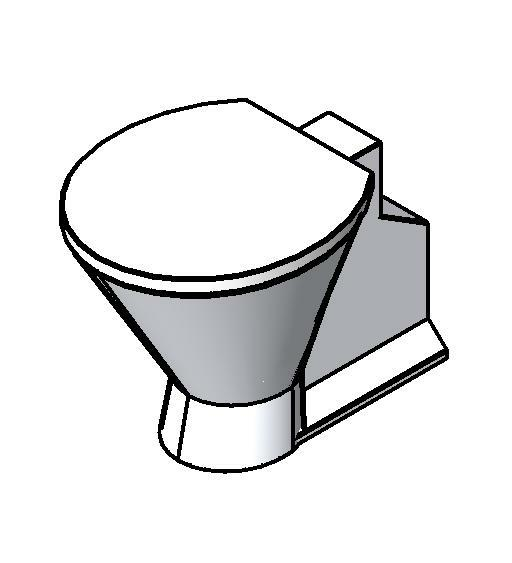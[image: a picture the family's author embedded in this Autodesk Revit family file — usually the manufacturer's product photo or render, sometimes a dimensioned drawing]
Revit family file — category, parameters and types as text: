
# Revit family: Deca_Cuba Semiencaixe retangular 40cm _Cuba Slim_L.63040
name_source: partatom
category: Plumbing Fixtures
units: mm (PartAtom-declared; Revit-internal decimal feet)

## family parameters
Cut with Voids When Loaded = No
Host = Face
Part Type = Normal
Room Calculation Point = No
Round Connector Dimension = Use Radius
Shared = No

## types (1)
- L.63040.17_Branco
    Acompanha o Produto = Acabamento da válvula cerâmica/Smartblock
    Aprovado por = quattroD
    Atendimento ao Cliente = 0800-0117073
    CWFU = 0
    Categoria = CUBAS
    Composição Básica = Composição Básica: Argila / Feldispato / Caulim / Vidrados e corantes inorgânicos / Plásticos de Engenharia.
    Composição Componente = PEBD
    Cor Interna = Branco
    Cor Principal = Branco
    Cores Componente = transparente
    Criado por = quattroD
    Código Pai = L.63040.17
    Default Elevation = 0 m
    Diâmetro Ponto de Esgoto = 0 m
    Diâmetro Água Fria = 0 m
    Informações Complementares = Esmalte Protekto
    Linha = CUBA SLIM
    Manufacturer = DECA
    Material = Deca_Branco
    Model = L.63040.17
    Norma = NBR 16728-1 / NBR 16728-2
    Peso Líquido (Kg) = 7.4
    Pressão máx. funcionamento = 40mca
    Pressão mín. funcionamento = 3mca
    Raio Ponto de Esgoto = 0 m
    Raio Água Fria = 0 m
    Saída de Esgoto = válvula curta
    Segmento = LUXO
    URL = www.deca.com.br
    WFU = 0

## geometry (parser evidence)
native form markers: Sweep x3
no freeform markers — native parametric forms only
